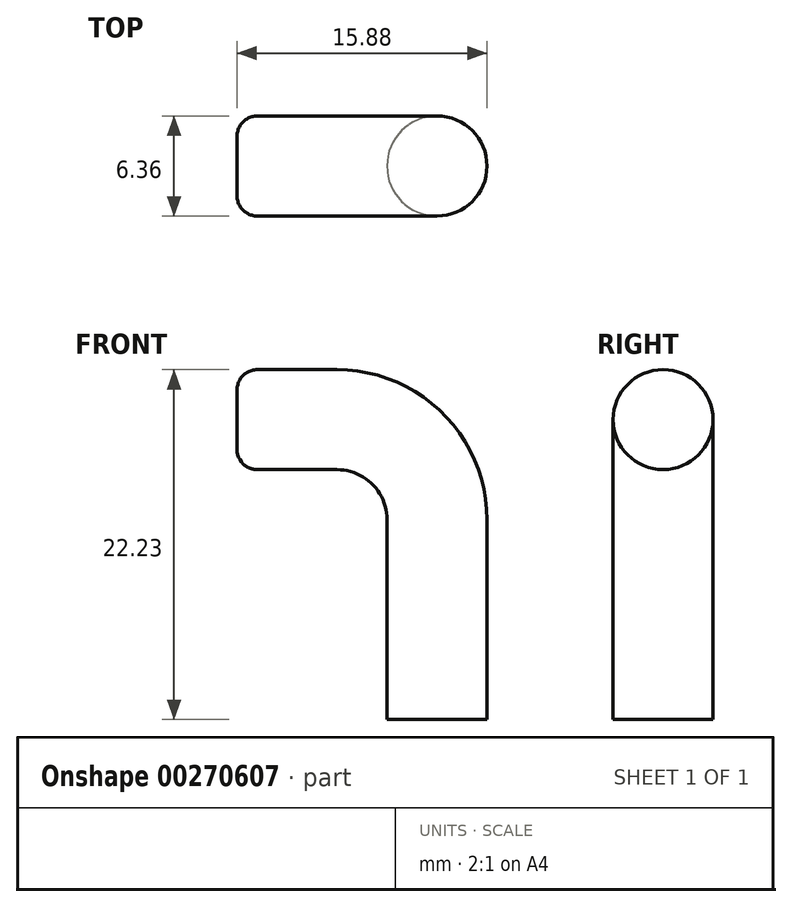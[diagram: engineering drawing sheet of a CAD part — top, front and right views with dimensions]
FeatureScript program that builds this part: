
annotation { "Feature Type Name" : "Feature", "Feature Type Description" : "" }
export const myFeature = defineFeature(function(context is Context, id is Id, definition is map)
    precondition{}
    {
        {
            var Q0;
            Q0=qCreatedBy(makeId("Top.planeOp"),FACE);
            var sketch = newSketch(context, id + "F0", { "sketchPlane" : qUnion([Q0])});
            skCircle(sketch, "E0", {"center": v(0, 0) * mm, "radius": 3.18 * mm});
            skSolve(sketch);
        }
        {
            var Q0;
            Q0=qCreatedBy(makeId("Front.planeOp"),FACE);
            var sketch = newSketch(context, id + "F1", { "sketchPlane" : qUnion([Q0])});
            skLineSegment(sketch, "E1", {"start": v(0, 0) * mm, "end": v(0, 12.7) * mm});
            skArc(sketch, "E2", {"start": v(0, 12.7) * mm, "mid": v(-1.86, 17.2) * mm, "end": v(-6.35, 19.05) * mm});
            skLineSegment(sketch, "E3", {"start": v(-6.35, 19.05) * mm, "end": v(-12.7, 19.05) * mm});
            skSolve(sketch);
        }
        {
            var Q0;
            Q0=makeQuery(id+"F0.imprint","IMPRINT",FACE,{"disambiguationData":[TD([[makeQuery(id+"F0.imprint","IMPRINT",EDGE,{"derivedFrom":sQuery(id+"F0.wireOp",EDGE,"E0")}),1.0]])]});
            var Q1;
            Q1=sQuery(id+"F1.wireOp",EDGE,"E1");
            var Q2;
            Q2=sQuery(id+"F1.wireOp",EDGE,"aUXW1Hrt-9nC9-R6G9-JWCm-2Hwvy9HD2dKM");
            var Q3;
            Q3=sQuery(id+"F1.wireOp",EDGE,"E2");
            var Q4;
            Q4=sQuery(id+"F1.wireOp",EDGE,"E3");
            sweep(context, id + "F2", {"profiles" : qUnion([Q0]), "path" : qUnion([Q1, Q2, Q3, Q4])});
        }
        {
            var Q0;
            Q0=makeQuery(id+"F2.opSweep","CAP_EDGE",EDGE,{"disambiguationData":[OSD([sQuery(id+"F0.wireOp",EDGE,"E0"),sQuery(id+"F1.wireOp",VERTEX,"aUXW1Hrt-9nC9-R6G9-JWCm-2Hwvy9HD2dKM.end")])],"isStart":false});
            fillet(context, id + "F3", {"entities" : qUnion([Q0]), "radius" : 1.29 * mm, "tangentPropagation" : true, "allowEdgeOverflow" : false});
        }
    });
